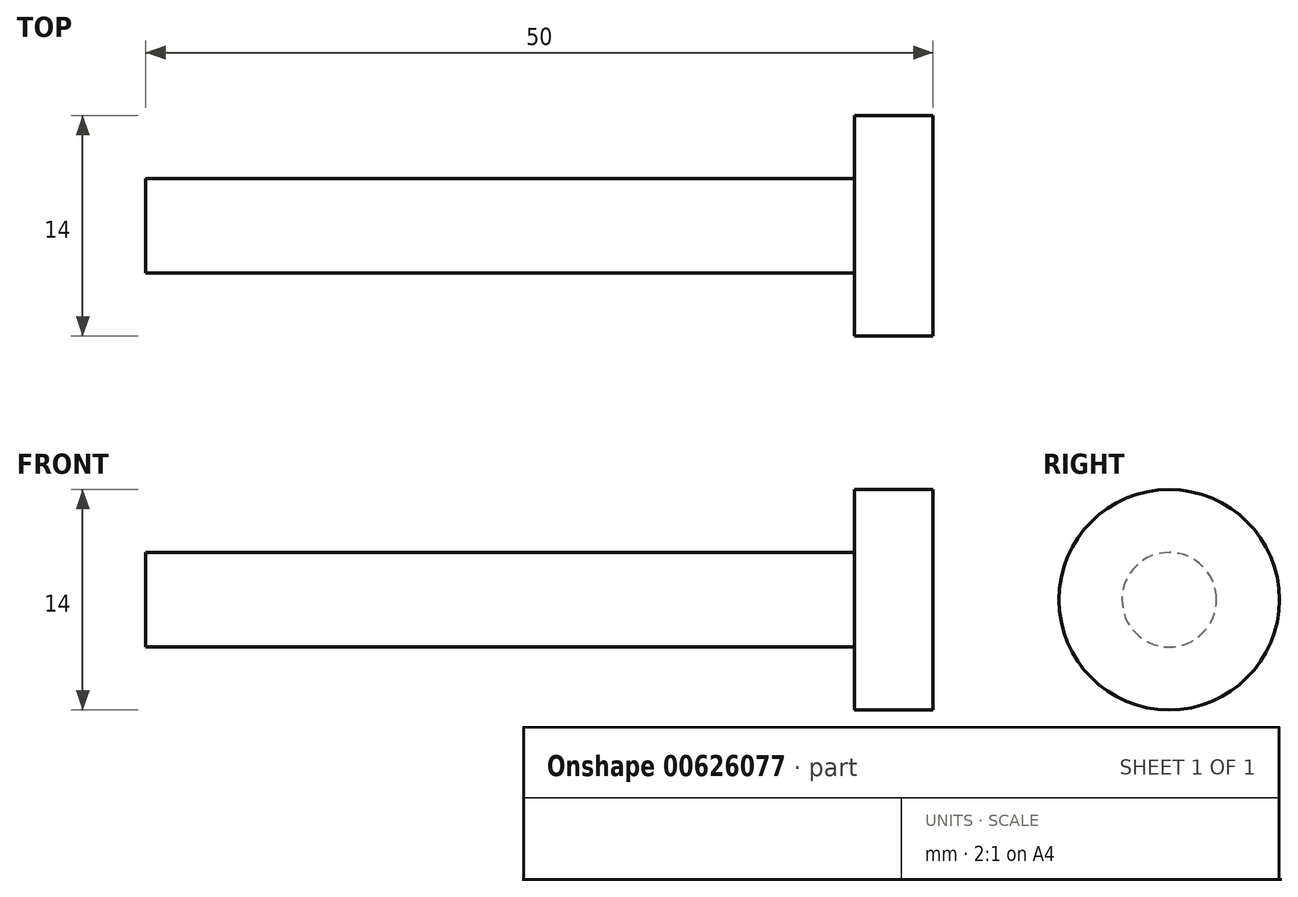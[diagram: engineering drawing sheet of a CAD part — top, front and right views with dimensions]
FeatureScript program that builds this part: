
annotation { "Feature Type Name" : "Feature", "Feature Type Description" : "" }
export const myFeature = defineFeature(function(context is Context, id is Id, definition is map)
    precondition{}
    {
        {
            var Q0;
            Q0=qCreatedBy(makeId("Front.planeOp"),FACE);
            var sketch = newSketch(context, id + "F0", { "sketchPlane" : qUnion([Q0])});
            skLineSegment(sketch, "E0", {"start": v(0, 7) * mm, "end": v(0, 0) * mm});
            skLineSegment(sketch, "E1", {"start": v(0, 0) * mm, "end": v(-50, 0) * mm});
            skLineSegment(sketch, "E2", {"start": v(-50, 0) * mm, "end": v(-50, 3) * mm});
            skLineSegment(sketch, "E3", {"start": v(0, 0) * mm, "end": v(0, 0) * mm});
            skLineSegment(sketch, "E4", {"start": v(0, 7) * mm, "end": v(-5, 7) * mm});
            skLineSegment(sketch, "E5", {"start": v(-5, 7) * mm, "end": v(-5, 3) * mm});
            skLineSegment(sketch, "E6", {"start": v(-5, 3) * mm, "end": v(-50, 3) * mm});
            skSolve(sketch);
        }
        {
            var Q0;
            Q0=makeQuery(id+"F0.imprint","IMPRINT",FACE,{"disambiguationData":[TD([[makeQuery(id+"F0.imprint","IMPRINT",EDGE,{"derivedFrom":sQuery(id+"F0.wireOp",EDGE,"E0")}),-1.0]])]});
            var Q1;
            Q1=sQuery(id+"F0.wireOp",EDGE,"E1");
            revolve(context, id + "F1", {"surfaceOperationType" : NewSurfaceOperationType.NEW, "entities" : qUnion([Q0]), "axis" : qUnion([Q1]), "revolveType" : RevolveType.FULL});
        }
    });
